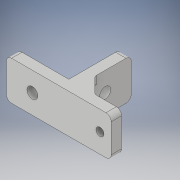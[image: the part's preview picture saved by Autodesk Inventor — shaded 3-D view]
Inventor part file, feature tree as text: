
AUTODESK INVENTOR PART (.ipt)
format: ipt  version: 2018 (Build 220112000, 112)  size: 171,520 bytes
history: native  units: in
note: dims shown in document units (in); Inventor stores cm internally (conversion verified against a paired STEP export)
features: sketch x7, extrude x6, fillet x3, projected_geometry x2, mirror x1
ambient origin geometry x8: Origin, YZ Plane, XZ Plane, XY Plane, X Axis, Y Axis, Z Axis, Center Point
bodies: Solid1 (feature_tree)
feature tree (19):
  extrude  "Extrusion1"  Depth=0.1575in
  extrude  "Extrusion2"  Depth=0.1575in
  extrude  "Extrusion3"  Depth=0.5906in TaperAngle=0.0deg
  extrude  "Extrusion4"  Depth=0.5906in TaperAngle=0.0deg
  extrude  "Extrusion5"  Depth=0.5906in TaperAngle=0.0deg
  mirror  "Mirror1"
  fillet  "Fillet1"  Radius=0.122in
  sketch  "Sketch6"  dims[d14=0.315in d15=0.5906in d16=0.0in d17=0.2362in d18=0.2362in]
  extrude  "Extrusion6"  Depth=0.5906in TaperAngle=0.0deg
  fillet  "Fillet2"  Radius=0.2362in
  fillet  "Fillet3"  Radius=0.2362in
  sketch  "Sketch1"  dims[d0=0.7874in d1=0.1575in]
  sketch  "Sketch2"  dims[d2=0.7874in d3=0.1575in]
  projected_geometry  "Projected Loop1"
  sketch  "Sketch3"  dims[d4=0.7874in d5=0.5906in d6=0.0in]
  projected_geometry  "Projected Loop2"
  sketch  "Sketch4"  dims[d7=0.1654in d8=0.5906in d9=0.0in]
  sketch  "Sketch5"  dims[d10=0.1654in d11=0.5906in d12=0.0in d13=0.122in]
  sketch  "Sketch7"  dims[d19=0.1181in d20=0.0in d21=0.0787in d22=0.1575in d23=0.0in d24=0.0787in d25=0.0787in]
